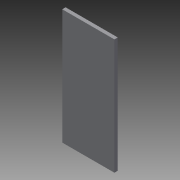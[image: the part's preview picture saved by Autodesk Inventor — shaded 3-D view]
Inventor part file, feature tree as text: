
AUTODESK INVENTOR PART (.ipt)
format: ipt  version: 2015 (Build 190159000, 159)  size: 67,584 bytes
history: native  units: mm
features: extrude x1, sketch x1
ambient origin geometry x8: Origin, YZ Plane, XZ Plane, XY Plane, X Axis, Y Axis, Z Axis, Center Point
bodies: Solid1 (feature_tree)
feature tree (2):
  extrude  "Extrusion1"  Depth=27.0mm
  sketch  "Sketch1"  dims[d0=59.75mm d1=27.0mm d2=1.75mm d3=0.0mm]
